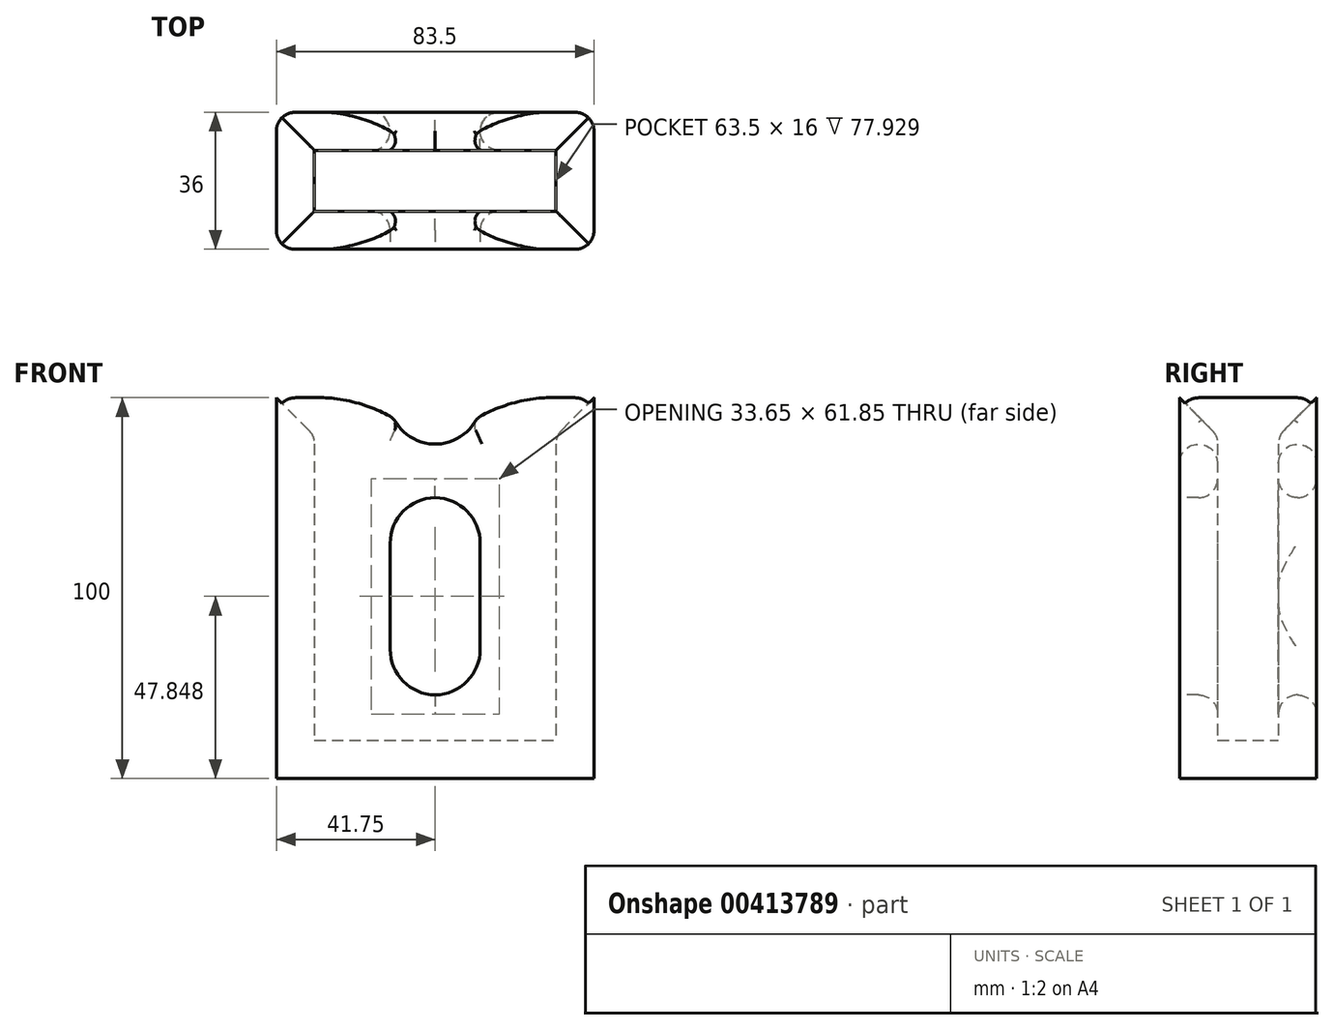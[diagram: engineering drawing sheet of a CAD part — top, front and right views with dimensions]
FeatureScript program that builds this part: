
annotation { "Feature Type Name" : "Feature", "Feature Type Description" : "" }
export const myFeature = defineFeature(function(context is Context, id is Id, definition is map)
    precondition{}
    {
        {
            var Q0;
            Q0=qCreatedBy(makeId("Front.planeOp"),FACE);
            var sketch = newSketch(context, id + "F0", { "sketchPlane" : qUnion([Q0])});
            skLineSegment(sketch, "E0.bottom", {"start": v(-31.75, 45) * mm, "end": v(31.75, 45) * mm});
            skLineSegment(sketch, "E0.top", {"start": v(-31.75, -45) * mm, "end": v(31.75, -45) * mm});
            skLineSegment(sketch, "E0.left", {"start": v(-31.75, 45) * mm, "end": v(-31.75, -45) * mm});
            skLineSegment(sketch, "E0.right", {"start": v(31.75, 45) * mm, "end": v(31.75, -45) * mm});
            skCircle(sketch, "E1", {"center": v(0, 45) * mm, "radius": 12.18 * mm});
            skSolve(sketch);
        }
        {
            var Q0;
            Q0=makeQuery(id+"F0.imprint","IMPRINT",FACE,{"disambiguationData":[TD([[makeQuery(id+"F0.imprint","IMPRINT",EDGE,{"derivedFrom":sQuery(id+"F0.wireOp",EDGE,"E0.top")}),1.0]])]});
            extrude(context, id + "F1", {"entities" : qUnion([Q0]), "depth" : 16 * mm});
        }
        {
            var Q0;
            Q0=makeQuery(id+"F1.opExtrude","SWEPT_FACE",FACE,{"disambiguationData":[OSD([sQuery(id+"F0.wireOp",EDGE,"E1")])]});
            var Q1;
            {var subQ0=sQuery(id+"F0.wireOp",EDGE,"E0.bottom");Q1=makeQuery(id+"F1.opExtrude","SWEPT_FACE",FACE,{"disambiguationData":[OSD([subQ0]),TDD([makeQuery(id+"F0.imprint","IMPRINT",EDGE,{"disambiguationData":[TD([[makeQuery(id+"F0.imprint","INTERSECT",VERTEX,{"derivedFrom":[subQ0,sQuery(id+"F0.wireOp",EDGE,"E0.left")]}),-1.0]])],"derivedFrom":subQ0})])]});}
            var Q2;
            {var subQ0=sQuery(id+"F0.wireOp",EDGE,"E0.bottom");Q2=makeQuery(id+"F1.opExtrude","SWEPT_FACE",FACE,{"disambiguationData":[OSD([subQ0]),TDD([makeQuery(id+"F0.imprint","IMPRINT",EDGE,{"disambiguationData":[TD([[makeQuery(id+"F0.imprint","INTERSECT",VERTEX,{"derivedFrom":[subQ0,sQuery(id+"F0.wireOp",EDGE,"E0.right")]}),1.0]])],"derivedFrom":subQ0})])]});}
            shell(context, id + "F2", {"entities" : qUnion([Q0, Q1, Q2]), "thickness" : 10 * mm, "oppositeDirection" : true});
        }
        {
            var Q0;
            Q0=makeQuery(id+"F1.opExtrude","CAP_FACE",FACE,{"disambiguationData":[OSD([sQuery(id+"F0.wireOp",EDGE,"E0.bottom"),sQuery(id+"F0.wireOp",EDGE,"E0.top"),sQuery(id+"F0.wireOp",EDGE,"E0.left"),sQuery(id+"F0.wireOp",EDGE,"E0.right"),sQuery(id+"F0.wireOp",EDGE,"E1")])],"isStart":false});
            var sketch = newSketch(context, id + "F3", { "sketchPlane" : qUnion([Q0])});
            skLineSegment(sketch, "E2.bottom", {"start": v(-0.17, 18.77) * mm, "end": v(0.17, 18.77) * mm});
            skLineSegment(sketch, "E2.top", {"start": v(-0.17, -33.08) * mm, "end": v(0.17, -33.08) * mm});
            skLineSegment(sketch, "E2.left", {"start": v(-11.83, 6.77) * mm, "end": v(-11.83, -21.08) * mm});
            skLineSegment(sketch, "E2.right", {"start": v(11.83, 6.77) * mm, "end": v(11.83, -21.08) * mm});
            skPoint(sketch, "E3.visualSharp", {"position": v(-11.83, 18.77) * mm});
            skArc(sketch, "E3.filletArc", {"start": v(0.17, 18.77) * mm, "mid": v(-8.31, 15.26) * mm, "end": v(-11.83, 6.77) * mm});
            skPoint(sketch, "E4.visualSharp", {"position": v(11.83, 18.77) * mm});
            skArc(sketch, "E4.filletArc", {"start": v(11.83, 6.77) * mm, "mid": v(8.31, 15.26) * mm, "end": v(-0.17, 18.77) * mm});
            skPoint(sketch, "E5.visualSharp", {"position": v(11.83, -33.08) * mm});
            skArc(sketch, "E5.filletArc", {"start": v(-0.17, -33.08) * mm, "mid": v(8.31, -29.56) * mm, "end": v(11.83, -21.08) * mm});
            skPoint(sketch, "E6.visualSharp", {"position": v(-11.83, -33.08) * mm});
            skArc(sketch, "E6.filletArc", {"start": v(-11.83, -21.08) * mm, "mid": v(-8.31, -29.56) * mm, "end": v(0.17, -33.08) * mm});
            skLineSegment(sketch, "E7", {"start": v(41.75, 28.68) * mm, "end": v(-41.75, 28.68) * mm});
            skSolve(sketch);
        }
        {
            var Q0;
            {var subQ4=sQuery(id+"F3.wireOp",EDGE,"E2.left");Q0=makeQuery(id+"F3.imprint","IMPRINT",FACE,{"disambiguationData":[TD([[makeQuery(id+"F3.imprint","IMPRINT",EDGE,{"derivedFrom":subQ4}),1.0]])]});}
            extrude(context, id + "F4", {"entities" : qUnion([Q0]), "operationType" : NewBodyOperationType.REMOVE, "oppositeDirection" : true, "depth" : 42.4 * mm});
        }
        {
            var Q0;
            {var subQ0=sQuery(id+"F0.wireOp",EDGE,"E0.bottom");Q0=makeQuery(id+"F2.opShell","OFFSET_EDGE",EDGE,{"disambiguationData":[OSD([subQ0]),TDD([makeQuery(id+"F1.opExtrude","CAP_EDGE",EDGE,{"disambiguationData":[OSD([subQ0]),TDD([makeQuery(id+"F0.imprint","IMPRINT",EDGE,{"disambiguationData":[TD([[makeQuery(id+"F0.imprint","INTERSECT",VERTEX,{"derivedFrom":[subQ0,sQuery(id+"F0.wireOp",EDGE,"E0.left")]}),-1.0]])],"derivedFrom":subQ0})])],"isStart":true})])]});}
            var Q1;
            Q1=makeQuery(id+"F2.opShell","OFFSET_EDGE",EDGE,{"disambiguationData":[OSD([sQuery(id+"F0.wireOp",EDGE,"E0.bottom"),sQuery(id+"F0.wireOp",EDGE,"E0.right")])]});
            var Q2;
            {var subQ0=sQuery(id+"F0.wireOp",EDGE,"E0.bottom");Q2=makeQuery(id+"F2.opShell","OFFSET_EDGE",EDGE,{"disambiguationData":[OSD([subQ0]),TDD([makeQuery(id+"F1.opExtrude","CAP_EDGE",EDGE,{"disambiguationData":[OSD([subQ0]),TDD([makeQuery(id+"F0.imprint","IMPRINT",EDGE,{"disambiguationData":[TD([[makeQuery(id+"F0.imprint","INTERSECT",VERTEX,{"derivedFrom":[subQ0,sQuery(id+"F0.wireOp",EDGE,"E0.right")]}),1.0]])],"derivedFrom":subQ0})])],"isStart":false})])]});}
            var Q3;
            Q3=makeQuery(id+"F2.opShell","OFFSET_EDGE",EDGE,{"disambiguationData":[OSD([sQuery(id+"F0.wireOp",EDGE,"E0.bottom"),sQuery(id+"F0.wireOp",EDGE,"E0.left")])]});
            var Q4;
            {var subQ0=sQuery(id+"F0.wireOp",EDGE,"E0.bottom");Q4=makeQuery(id+"F2.opShell","OFFSET_EDGE",EDGE,{"disambiguationData":[OSD([subQ0]),TDD([makeQuery(id+"F1.opExtrude","CAP_EDGE",EDGE,{"disambiguationData":[OSD([subQ0]),TDD([makeQuery(id+"F0.imprint","IMPRINT",EDGE,{"disambiguationData":[TD([[makeQuery(id+"F0.imprint","INTERSECT",VERTEX,{"derivedFrom":[subQ0,sQuery(id+"F0.wireOp",EDGE,"E0.left")]}),-1.0]])],"derivedFrom":subQ0})])],"isStart":false})])]});}
            var Q5;
            {var subQ0=sQuery(id+"F0.wireOp",EDGE,"E0.bottom");Q5=makeQuery(id+"F2.opShell","OFFSET_EDGE",EDGE,{"disambiguationData":[OSD([subQ0]),TDD([makeQuery(id+"F1.opExtrude","CAP_EDGE",EDGE,{"disambiguationData":[OSD([subQ0]),TDD([makeQuery(id+"F0.imprint","IMPRINT",EDGE,{"disambiguationData":[TD([[makeQuery(id+"F0.imprint","INTERSECT",VERTEX,{"derivedFrom":[subQ0,sQuery(id+"F0.wireOp",EDGE,"E0.right")]}),1.0]])],"derivedFrom":subQ0})])],"isStart":true})])]});}
            var Q6;
            {var subQ0=sQuery(id+"F0.wireOp",EDGE,"E1");var subQ1=sQuery(id+"F0.wireOp",EDGE,"E0.bottom");Q6=makeQuery(id+"F2.opShell","OFFSET_EDGE",EDGE,{"disambiguationData":[OSD([subQ1,subQ0]),TDD([makeQuery(id+"F1.opExtrude","SWEPT_EDGE",EDGE,{"disambiguationData":[OSD([subQ1,subQ0]),TDD([makeQuery(id+"F0.imprint","INTERSECT",VERTEX,{"disambiguationData":[OD(1.0)],"derivedFrom":[subQ1,subQ0]})])]})])]});}
            var Q7;
            {var subQ0=sQuery(id+"F0.wireOp",EDGE,"E1");var subQ1=sQuery(id+"F0.wireOp",EDGE,"E0.bottom");Q7=makeQuery(id+"F2.opShell","OFFSET_EDGE",EDGE,{"disambiguationData":[OSD([subQ1,subQ0]),TDD([makeQuery(id+"F1.opExtrude","SWEPT_EDGE",EDGE,{"disambiguationData":[OSD([subQ1,subQ0]),TDD([makeQuery(id+"F0.imprint","INTERSECT",VERTEX,{"disambiguationData":[OD(0.0)],"derivedFrom":[subQ1,subQ0]})])]})])]});}
            var Q8;
            {var subQ0=sQuery(id+"F0.wireOp",EDGE,"E1");var subQ1=sQuery(id+"F0.wireOp",EDGE,"E0.bottom");Q8=makeQuery(id+"F1.opExtrude","SWEPT_EDGE",EDGE,{"disambiguationData":[OSD([subQ1,subQ0]),TDD([makeQuery(id+"F0.imprint","INTERSECT",VERTEX,{"disambiguationData":[OD(0.0)],"derivedFrom":[subQ1,subQ0]})])]});}
            var Q9;
            {var subQ0=sQuery(id+"F0.wireOp",EDGE,"E1");var subQ1=sQuery(id+"F0.wireOp",EDGE,"E0.bottom");Q9=makeQuery(id+"F1.opExtrude","SWEPT_EDGE",EDGE,{"disambiguationData":[OSD([subQ1,subQ0]),TDD([makeQuery(id+"F0.imprint","INTERSECT",VERTEX,{"disambiguationData":[OD(1.0)],"derivedFrom":[subQ1,subQ0]})])]});}
            chamfer(context, id + "F5", {"entities" : qUnion([Q0, Q1, Q2, Q3, Q4, Q5, Q6, Q7, Q8, Q9]), "width" : 10 * mm, "tangentPropagation" : true});
        }
        {
            var Q0;
            Q0=makeQuery(id+"F1.opExtrude","CAP_EDGE",EDGE,{"disambiguationData":[OSD([sQuery(id+"F0.wireOp",EDGE,"E0.right")])],"isStart":false});
            var Q1;
            Q1=makeQuery(id+"F1.opExtrude","CAP_EDGE",EDGE,{"disambiguationData":[OSD([sQuery(id+"F0.wireOp",EDGE,"E0.right")])],"isStart":true});
            var Q2;
            Q2=makeQuery(id+"F1.opExtrude","CAP_EDGE",EDGE,{"disambiguationData":[OSD([sQuery(id+"F0.wireOp",EDGE,"E0.left")])],"isStart":true});
            var Q3;
            Q3=makeQuery(id+"F1.opExtrude","CAP_EDGE",EDGE,{"disambiguationData":[OSD([sQuery(id+"F0.wireOp",EDGE,"E0.left")])],"isStart":false});
            var Q4;
            {var subQ0=sQuery(id+"F0.wireOp",EDGE,"E1");var subQ1=sQuery(id+"F0.wireOp",EDGE,"E0.right");var subQ2=sQuery(id+"F0.wireOp",EDGE,"E0.left");var subQ3=sQuery(id+"F0.wireOp",EDGE,"E0.top");var subQ4=sQuery(id+"F0.wireOp",EDGE,"E0.bottom");Q4=makeQuery(id+"F4.boolean.opBoolean","INTERSECT",EDGE,{"derivedFrom":[makeQuery(id+"F2.opShell","OFFSET_FACE",FACE,{"disambiguationData":[OSD([subQ4,subQ3,subQ2,subQ1,subQ0]),TDD([makeQuery(id+"F1.opExtrude","CAP_FACE",FACE,{"disambiguationData":[OSD([subQ4,subQ3,subQ2,subQ1,subQ0])],"isStart":false})])]}),makeQuery(id+"F4.opExtrude","SWEPT_FACE",FACE,{"disambiguationData":[OSD([sQuery(id+"F3.wireOp",EDGE,"E2.right")])]})]});}
            var Q5;
            Q5=makeQuery(id+"F4.boolean.opBoolean","COPY",EDGE,{"derivedFrom":makeQuery(id+"F4.opExtrude","CAP_EDGE",EDGE,{"disambiguationData":[OSD([sQuery(id+"F3.wireOp",EDGE,"E2.right")])],"isStart":true})});
            var Q6;
            Q6=makeQuery(id+"F4.boolean.opBoolean","COPY",EDGE,{"derivedFrom":makeQuery(id+"F4.opExtrude","CAP_EDGE",EDGE,{"disambiguationData":[OSD([sQuery(id+"F3.wireOp",EDGE,"E2.left")])],"isStart":true})});
            var Q7;
            {var subQ0=sQuery(id+"F0.wireOp",EDGE,"E1");var subQ1=sQuery(id+"F0.wireOp",EDGE,"E0.right");var subQ2=sQuery(id+"F0.wireOp",EDGE,"E0.left");var subQ3=sQuery(id+"F0.wireOp",EDGE,"E0.top");var subQ4=sQuery(id+"F0.wireOp",EDGE,"E0.bottom");Q7=makeQuery(id+"F4.boolean.opBoolean","INTERSECT",EDGE,{"derivedFrom":[makeQuery(id+"F2.opShell","OFFSET_FACE",FACE,{"disambiguationData":[OSD([subQ4,subQ3,subQ2,subQ1,subQ0]),TDD([makeQuery(id+"F1.opExtrude","CAP_FACE",FACE,{"disambiguationData":[OSD([subQ4,subQ3,subQ2,subQ1,subQ0])],"isStart":false})])]}),makeQuery(id+"F4.opExtrude","SWEPT_FACE",FACE,{"disambiguationData":[OSD([sQuery(id+"F3.wireOp",EDGE,"E2.left")])]})]});}
            var Q8;
            {var subQ0=sQuery(id+"F0.wireOp",EDGE,"E1");var subQ1=sQuery(id+"F0.wireOp",EDGE,"E0.right");var subQ2=sQuery(id+"F0.wireOp",EDGE,"E0.left");var subQ3=sQuery(id+"F0.wireOp",EDGE,"E0.top");var subQ4=sQuery(id+"F0.wireOp",EDGE,"E0.bottom");Q8=makeQuery(id+"F4.boolean.opBoolean","INTERSECT",EDGE,{"derivedFrom":[makeQuery(id+"F2.opShell","OFFSET_FACE",FACE,{"disambiguationData":[OSD([subQ4,subQ3,subQ2,subQ1,subQ0]),TDD([makeQuery(id+"F1.opExtrude","CAP_FACE",FACE,{"disambiguationData":[OSD([subQ4,subQ3,subQ2,subQ1,subQ0])],"isStart":true})])]}),makeQuery(id+"F4.opExtrude","SWEPT_FACE",FACE,{"disambiguationData":[OSD([sQuery(id+"F3.wireOp",EDGE,"E2.left")])]})]});}
            var Q9;
            Q9=makeQuery(id+"F4.boolean.opBoolean","INTERSECT",EDGE,{"derivedFrom":[makeQuery(id+"F1.opExtrude","CAP_FACE",FACE,{"disambiguationData":[OSD([sQuery(id+"F0.wireOp",EDGE,"E0.bottom"),sQuery(id+"F0.wireOp",EDGE,"E0.top"),sQuery(id+"F0.wireOp",EDGE,"E0.left"),sQuery(id+"F0.wireOp",EDGE,"E0.right"),sQuery(id+"F0.wireOp",EDGE,"E1")])],"isStart":true}),makeQuery(id+"F4.opExtrude","SWEPT_FACE",FACE,{"disambiguationData":[OSD([sQuery(id+"F3.wireOp",EDGE,"E2.left")])]})]});
            var Q10;
            Q10=makeQuery(id+"F4.boolean.opBoolean","INTERSECT",EDGE,{"derivedFrom":[makeQuery(id+"F1.opExtrude","CAP_FACE",FACE,{"disambiguationData":[OSD([sQuery(id+"F0.wireOp",EDGE,"E0.bottom"),sQuery(id+"F0.wireOp",EDGE,"E0.top"),sQuery(id+"F0.wireOp",EDGE,"E0.left"),sQuery(id+"F0.wireOp",EDGE,"E0.right"),sQuery(id+"F0.wireOp",EDGE,"E1")])],"isStart":true}),makeQuery(id+"F4.opExtrude","SWEPT_FACE",FACE,{"disambiguationData":[OSD([sQuery(id+"F3.wireOp",EDGE,"E2.right")])]})]});
            var Q11;
            {var subQ0=sQuery(id+"F0.wireOp",EDGE,"E1");Q11=makeQuery(id+"F2.opShell","OFFSET_EDGE",EDGE,{"disambiguationData":[OSD([subQ0]),TDD([makeQuery(id+"F1.opExtrude","CAP_EDGE",EDGE,{"disambiguationData":[OSD([subQ0])],"isStart":true})])]});}
            var Q12;
            {var subQ0=sQuery(id+"F0.wireOp",EDGE,"E1");var subQ1=sQuery(id+"F0.wireOp",EDGE,"E0.right");var subQ2=sQuery(id+"F0.wireOp",EDGE,"E0.left");var subQ3=sQuery(id+"F0.wireOp",EDGE,"E0.top");var subQ4=sQuery(id+"F0.wireOp",EDGE,"E0.bottom");Q12=makeQuery(id+"F5.opChamfer","BLEND_EDGE",EDGE,{"blendedFrom":[makeQuery(id+"F2.opShell","OFFSET_EDGE",EDGE,{"disambiguationData":[OSD([subQ4]),TDD([makeQuery(id+"F1.opExtrude","CAP_EDGE",EDGE,{"disambiguationData":[OSD([subQ4]),TDD([makeQuery(id+"F0.imprint","IMPRINT",EDGE,{"disambiguationData":[TD([[makeQuery(id+"F0.imprint","INTERSECT",VERTEX,{"derivedFrom":[subQ4,subQ1]}),1.0]])],"derivedFrom":subQ4})])],"isStart":true})])]}),makeQuery(id+"F2.opShell","OFFSET_FACE",FACE,{"disambiguationData":[OSD([subQ4,subQ3,subQ2,subQ1,subQ0]),TDD([makeQuery(id+"F1.opExtrude","CAP_FACE",FACE,{"disambiguationData":[OSD([subQ4,subQ3,subQ2,subQ1,subQ0])],"isStart":true})])]})],"blendedInto":[makeQuery(id+"F2.opShell","OFFSET_FACE",FACE,{"disambiguationData":[OSD([subQ4,subQ3,subQ2,subQ1,subQ0]),TDD([makeQuery(id+"F1.opExtrude","CAP_FACE",FACE,{"disambiguationData":[OSD([subQ4,subQ3,subQ2,subQ1,subQ0])],"isStart":true})])]})]});}
            var Q13;
            {var subQ0=sQuery(id+"F0.wireOp",EDGE,"E1");var subQ1=sQuery(id+"F0.wireOp",EDGE,"E0.right");var subQ2=sQuery(id+"F0.wireOp",EDGE,"E0.left");var subQ3=sQuery(id+"F0.wireOp",EDGE,"E0.top");var subQ4=sQuery(id+"F0.wireOp",EDGE,"E0.bottom");Q13=makeQuery(id+"F5.opChamfer","BLEND_EDGE",EDGE,{"blendedFrom":[makeQuery(id+"F2.opShell","OFFSET_EDGE",EDGE,{"disambiguationData":[OSD([subQ4]),TDD([makeQuery(id+"F1.opExtrude","CAP_EDGE",EDGE,{"disambiguationData":[OSD([subQ4]),TDD([makeQuery(id+"F0.imprint","IMPRINT",EDGE,{"disambiguationData":[TD([[makeQuery(id+"F0.imprint","INTERSECT",VERTEX,{"derivedFrom":[subQ4,subQ2]}),-1.0]])],"derivedFrom":subQ4})])],"isStart":true})])]}),makeQuery(id+"F2.opShell","OFFSET_FACE",FACE,{"disambiguationData":[OSD([subQ4,subQ3,subQ2,subQ1,subQ0]),TDD([makeQuery(id+"F1.opExtrude","CAP_FACE",FACE,{"disambiguationData":[OSD([subQ4,subQ3,subQ2,subQ1,subQ0])],"isStart":true})])]})],"blendedInto":[makeQuery(id+"F2.opShell","OFFSET_FACE",FACE,{"disambiguationData":[OSD([subQ4,subQ3,subQ2,subQ1,subQ0]),TDD([makeQuery(id+"F1.opExtrude","CAP_FACE",FACE,{"disambiguationData":[OSD([subQ4,subQ3,subQ2,subQ1,subQ0])],"isStart":true})])]})]});}
            var Q14;
            {var subQ0=sQuery(id+"F0.wireOp",EDGE,"E0.right");Q14=makeQuery(id+"F5.opChamfer","BLEND_EDGE",EDGE,{"blendedFrom":[makeQuery(id+"F2.opShell","OFFSET_EDGE",EDGE,{"disambiguationData":[OSD([sQuery(id+"F0.wireOp",EDGE,"E0.bottom"),subQ0])]}),makeQuery(id+"F2.opShell","OFFSET_FACE",FACE,{"disambiguationData":[OSD([subQ0])]})],"blendedInto":[makeQuery(id+"F2.opShell","OFFSET_FACE",FACE,{"disambiguationData":[OSD([subQ0])]})]});}
            var Q15;
            {var subQ0=sQuery(id+"F0.wireOp",EDGE,"E1");var subQ1=sQuery(id+"F0.wireOp",EDGE,"E0.right");var subQ2=sQuery(id+"F0.wireOp",EDGE,"E0.left");var subQ3=sQuery(id+"F0.wireOp",EDGE,"E0.top");var subQ4=sQuery(id+"F0.wireOp",EDGE,"E0.bottom");Q15=makeQuery(id+"F5.opChamfer","BLEND_EDGE",EDGE,{"blendedFrom":[makeQuery(id+"F2.opShell","OFFSET_EDGE",EDGE,{"disambiguationData":[OSD([subQ4]),TDD([makeQuery(id+"F1.opExtrude","CAP_EDGE",EDGE,{"disambiguationData":[OSD([subQ4]),TDD([makeQuery(id+"F0.imprint","IMPRINT",EDGE,{"disambiguationData":[TD([[makeQuery(id+"F0.imprint","INTERSECT",VERTEX,{"derivedFrom":[subQ4,subQ1]}),1.0]])],"derivedFrom":subQ4})])],"isStart":false})])]}),makeQuery(id+"F2.opShell","OFFSET_FACE",FACE,{"disambiguationData":[OSD([subQ4,subQ3,subQ2,subQ1,subQ0]),TDD([makeQuery(id+"F1.opExtrude","CAP_FACE",FACE,{"disambiguationData":[OSD([subQ4,subQ3,subQ2,subQ1,subQ0])],"isStart":false})])]})],"blendedInto":[makeQuery(id+"F2.opShell","OFFSET_FACE",FACE,{"disambiguationData":[OSD([subQ4,subQ3,subQ2,subQ1,subQ0]),TDD([makeQuery(id+"F1.opExtrude","CAP_FACE",FACE,{"disambiguationData":[OSD([subQ4,subQ3,subQ2,subQ1,subQ0])],"isStart":false})])]})]});}
            var Q16;
            {var subQ0=sQuery(id+"F0.wireOp",EDGE,"E1");Q16=makeQuery(id+"F2.opShell","OFFSET_EDGE",EDGE,{"disambiguationData":[OSD([subQ0]),TDD([makeQuery(id+"F1.opExtrude","CAP_EDGE",EDGE,{"disambiguationData":[OSD([subQ0])],"isStart":false})])]});}
            var Q17;
            {var subQ0=sQuery(id+"F0.wireOp",EDGE,"E1");var subQ1=sQuery(id+"F0.wireOp",EDGE,"E0.right");var subQ2=sQuery(id+"F0.wireOp",EDGE,"E0.left");var subQ3=sQuery(id+"F0.wireOp",EDGE,"E0.top");var subQ4=sQuery(id+"F0.wireOp",EDGE,"E0.bottom");Q17=makeQuery(id+"F5.opChamfer","BLEND_EDGE",EDGE,{"blendedFrom":[makeQuery(id+"F2.opShell","OFFSET_EDGE",EDGE,{"disambiguationData":[OSD([subQ4]),TDD([makeQuery(id+"F1.opExtrude","CAP_EDGE",EDGE,{"disambiguationData":[OSD([subQ4]),TDD([makeQuery(id+"F0.imprint","IMPRINT",EDGE,{"disambiguationData":[TD([[makeQuery(id+"F0.imprint","INTERSECT",VERTEX,{"derivedFrom":[subQ4,subQ2]}),-1.0]])],"derivedFrom":subQ4})])],"isStart":false})])]}),makeQuery(id+"F2.opShell","OFFSET_FACE",FACE,{"disambiguationData":[OSD([subQ4,subQ3,subQ2,subQ1,subQ0]),TDD([makeQuery(id+"F1.opExtrude","CAP_FACE",FACE,{"disambiguationData":[OSD([subQ4,subQ3,subQ2,subQ1,subQ0])],"isStart":false})])]})],"blendedInto":[makeQuery(id+"F2.opShell","OFFSET_FACE",FACE,{"disambiguationData":[OSD([subQ4,subQ3,subQ2,subQ1,subQ0]),TDD([makeQuery(id+"F1.opExtrude","CAP_FACE",FACE,{"disambiguationData":[OSD([subQ4,subQ3,subQ2,subQ1,subQ0])],"isStart":false})])]})]});}
            var Q18;
            {var subQ0=sQuery(id+"F0.wireOp",EDGE,"E1");var subQ1=sQuery(id+"F0.wireOp",EDGE,"E0.bottom");Q18=makeQuery(id+"F5.opChamfer","BLEND_EDGE",EDGE,{"blendedFrom":[makeQuery(id+"F1.opExtrude","SWEPT_EDGE",EDGE,{"disambiguationData":[OSD([subQ1,subQ0]),TDD([makeQuery(id+"F0.imprint","INTERSECT",VERTEX,{"disambiguationData":[OD(0.0)],"derivedFrom":[subQ1,subQ0]})])]}),makeQuery(id+"F1.opExtrude","SWEPT_FACE",FACE,{"disambiguationData":[OSD([subQ0])]})],"blendedInto":[makeQuery(id+"F1.opExtrude","SWEPT_FACE",FACE,{"disambiguationData":[OSD([subQ0])]})]});}
            var Q19;
            {var subQ0=sQuery(id+"F0.wireOp",EDGE,"E1");var subQ1=sQuery(id+"F0.wireOp",EDGE,"E0.bottom");Q19=makeQuery(id+"F5.opChamfer","BLEND_EDGE",EDGE,{"blendedFrom":[makeQuery(id+"F2.opShell","OFFSET_EDGE",EDGE,{"disambiguationData":[OSD([subQ1,subQ0]),TDD([makeQuery(id+"F1.opExtrude","SWEPT_EDGE",EDGE,{"disambiguationData":[OSD([subQ1,subQ0]),TDD([makeQuery(id+"F0.imprint","INTERSECT",VERTEX,{"disambiguationData":[OD(0.0)],"derivedFrom":[subQ1,subQ0]})])]})])]}),makeQuery(id+"F2.opShell","OFFSET_FACE",FACE,{"disambiguationData":[OSD([subQ0])]})],"blendedInto":[makeQuery(id+"F2.opShell","OFFSET_FACE",FACE,{"disambiguationData":[OSD([subQ0])]})]});}
            var Q20;
            {var subQ0=sQuery(id+"F0.wireOp",EDGE,"E1");var subQ1=sQuery(id+"F0.wireOp",EDGE,"E0.bottom");Q20=makeQuery(id+"F5.opChamfer","BLEND_EDGE",EDGE,{"blendedFrom":[makeQuery(id+"F2.opShell","OFFSET_EDGE",EDGE,{"disambiguationData":[OSD([subQ1,subQ0]),TDD([makeQuery(id+"F1.opExtrude","SWEPT_EDGE",EDGE,{"disambiguationData":[OSD([subQ1,subQ0]),TDD([makeQuery(id+"F0.imprint","INTERSECT",VERTEX,{"disambiguationData":[OD(1.0)],"derivedFrom":[subQ1,subQ0]})])]})])]}),makeQuery(id+"F2.opShell","OFFSET_FACE",FACE,{"disambiguationData":[OSD([subQ0])]})],"blendedInto":[makeQuery(id+"F2.opShell","OFFSET_FACE",FACE,{"disambiguationData":[OSD([subQ0])]})]});}
            var Q21;
            {var subQ0=sQuery(id+"F0.wireOp",EDGE,"E1");var subQ1=sQuery(id+"F0.wireOp",EDGE,"E0.bottom");Q21=makeQuery(id+"F5.opChamfer","BLEND_EDGE",EDGE,{"blendedFrom":[makeQuery(id+"F1.opExtrude","SWEPT_EDGE",EDGE,{"disambiguationData":[OSD([subQ1,subQ0]),TDD([makeQuery(id+"F0.imprint","INTERSECT",VERTEX,{"disambiguationData":[OD(1.0)],"derivedFrom":[subQ1,subQ0]})])]}),makeQuery(id+"F1.opExtrude","SWEPT_FACE",FACE,{"disambiguationData":[OSD([subQ0])]})],"blendedInto":[makeQuery(id+"F1.opExtrude","SWEPT_FACE",FACE,{"disambiguationData":[OSD([subQ0])]})]});}
            var Q22;
            {var subQ0=sQuery(id+"F0.wireOp",EDGE,"E0.left");Q22=makeQuery(id+"F5.opChamfer","BLEND_EDGE",EDGE,{"blendedFrom":[makeQuery(id+"F2.opShell","OFFSET_EDGE",EDGE,{"disambiguationData":[OSD([sQuery(id+"F0.wireOp",EDGE,"E0.bottom"),subQ0])]}),makeQuery(id+"F2.opShell","OFFSET_FACE",FACE,{"disambiguationData":[OSD([subQ0])]})],"blendedInto":[makeQuery(id+"F2.opShell","OFFSET_FACE",FACE,{"disambiguationData":[OSD([subQ0])]})]});}
            fillet(context, id + "F6", {"entities" : qUnion([Q0, Q1, Q2, Q3, Q4, Q5, Q6, Q7, Q8, Q9, Q10, Q11, Q12, Q13, Q14, Q15, Q16, Q17, Q18, Q19, Q20, Q21, Q22]), "radius" : 5 * mm, "tangentPropagation" : true, "allowEdgeOverflow" : false});
        }
        {
            var Q0;
            Q0=makeQuery(id+"F1.opExtrude","CAP_EDGE",EDGE,{"disambiguationData":[OSD([sQuery(id+"F0.wireOp",EDGE,"E1")])],"isStart":true});
            var Q1;
            Q1=makeQuery(id+"F1.opExtrude","CAP_EDGE",EDGE,{"disambiguationData":[OSD([sQuery(id+"F0.wireOp",EDGE,"E1")])],"isStart":false});
            fillet(context, id + "F7", {"entities" : qUnion([Q0, Q1]), "radius" : 5 * mm, "tangentPropagation" : true, "allowEdgeOverflow" : false});
        }
    });
